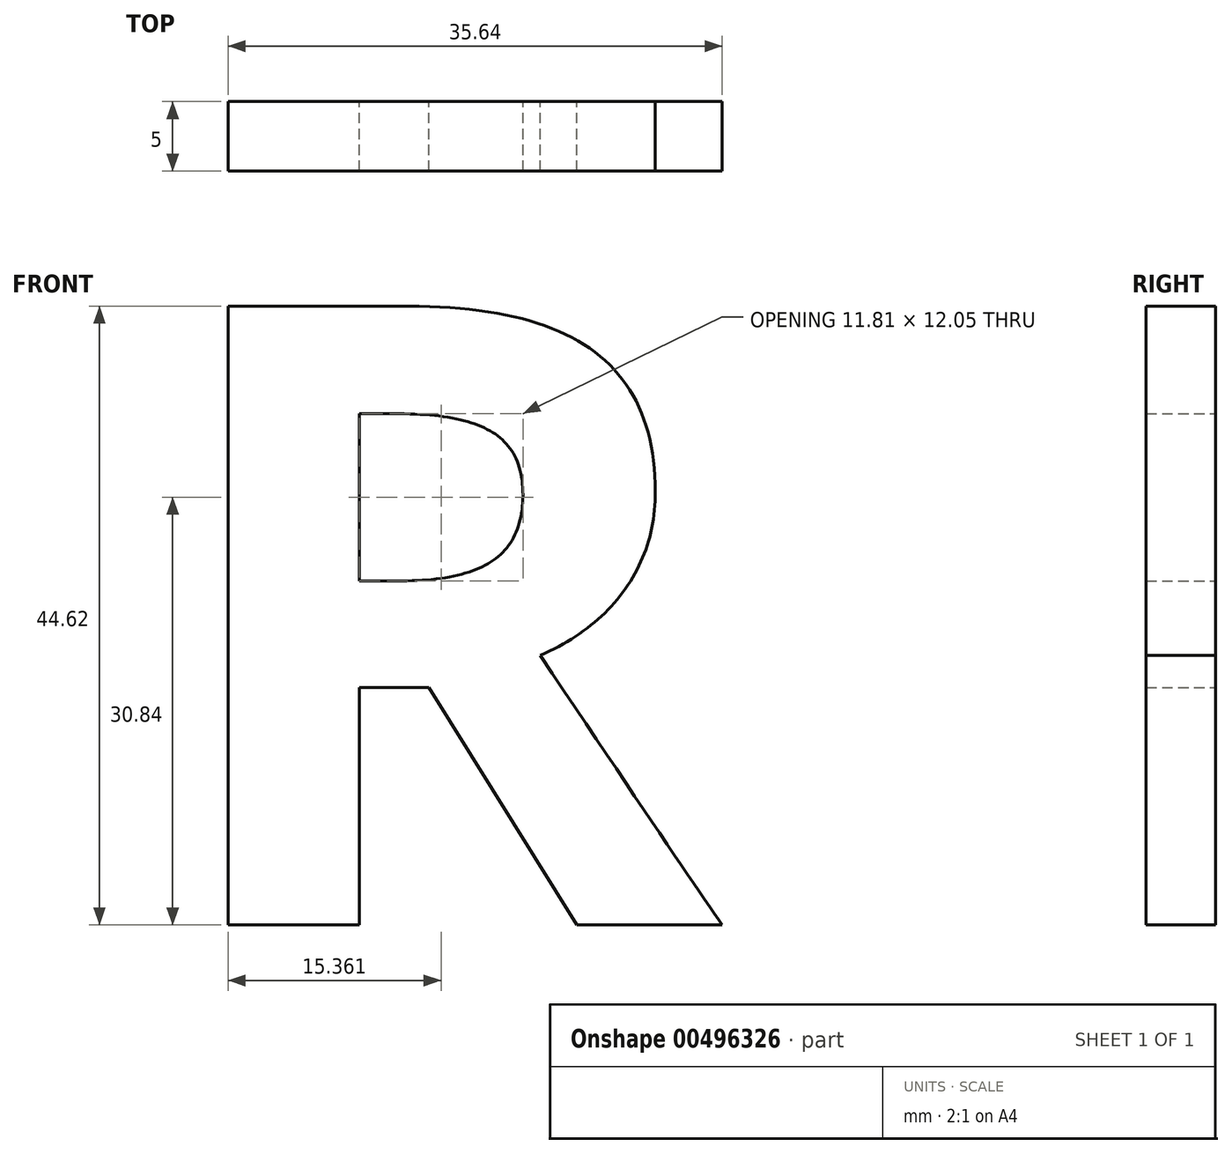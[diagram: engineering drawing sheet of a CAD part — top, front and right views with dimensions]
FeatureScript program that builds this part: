
annotation { "Feature Type Name" : "Feature", "Feature Type Description" : "" }
export const myFeature = defineFeature(function(context is Context, id is Id, definition is map)
    precondition{}
    {
        {
            var Q0;
            Q0=qCreatedBy(makeId("Front.planeOp"),FACE);
            var sketch = newSketch(context, id + "F0", { "sketchPlane" : qUnion([Q0])});
            skText(sketch, "E0", { "text": "R", "fontName": "OpenSans-Bold.ttf"});
            const initialGuessF0  = {"E0": [-0.06004, 0.01208, 1, 0, 0.045]};
            skSetInitialGuess(sketch, initialGuessF0);
            skSolve(sketch);
        }
        {
            var Q0;
            Q0=makeQuery(id+"F0.imprint","IMPRINT",FACE,{"disambiguationData":[TD([[makeQuery(id+"F0.imprint","IMPRINT",EDGE,{"derivedFrom":sQuery(id+"F0.wireOp",EDGE,"E0.sketch_text.stroke-0")}),-1.0]])]});
            extrude(context, id + "F1", {"entities" : qUnion([Q0]), "depth" : 5 * mm});
        }
    });
